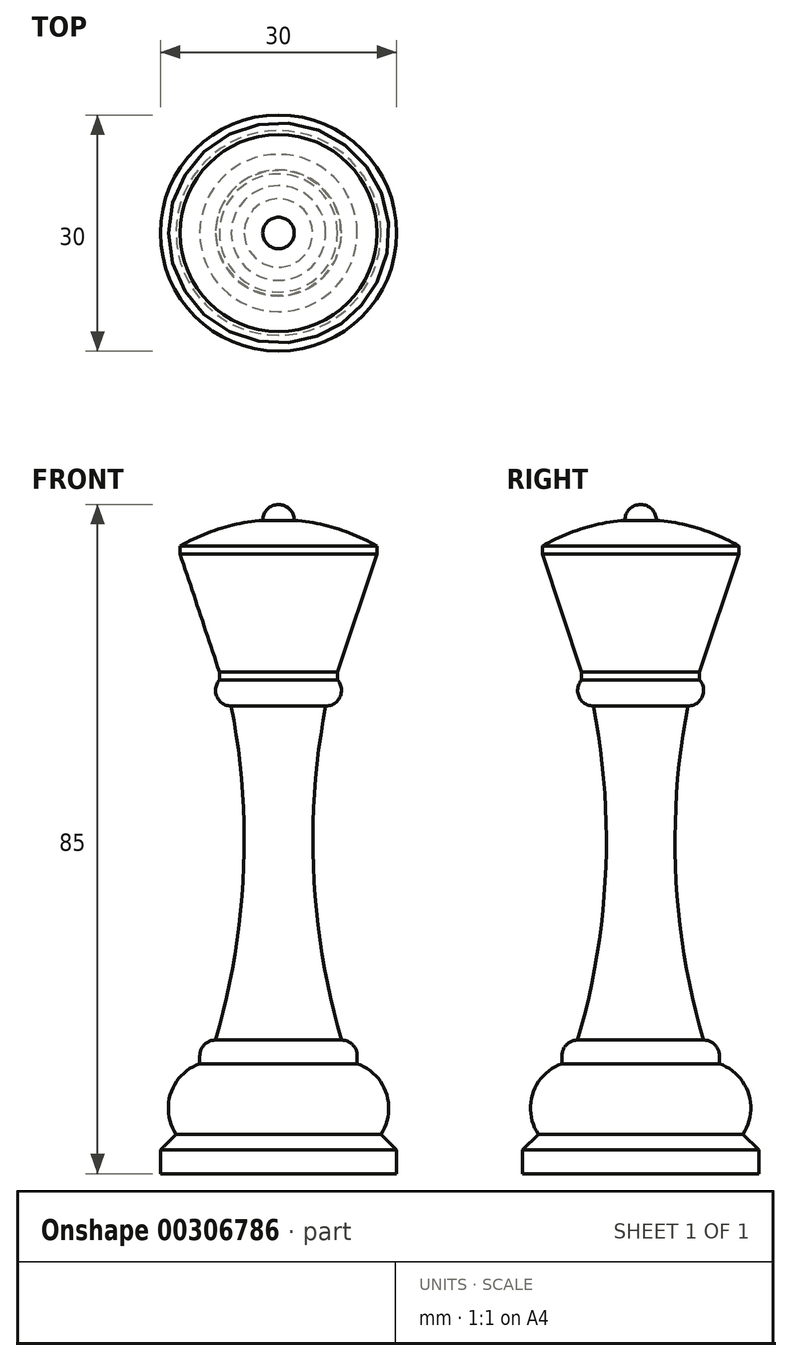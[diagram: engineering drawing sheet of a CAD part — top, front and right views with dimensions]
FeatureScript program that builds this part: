
annotation { "Feature Type Name" : "Feature", "Feature Type Description" : "" }
export const myFeature = defineFeature(function(context is Context, id is Id, definition is map)
    precondition{}
    {
        {
            var Q0;
            Q0=qCreatedBy(makeId("Front.planeOp"),FACE);
            var sketch = newSketch(context, id + "F0", { "sketchPlane" : qUnion([Q0])});
            skArc(sketch, "E0", {"start": v(2, -2) * mm, "mid": v(1.41, -0.59) * mm, "end": v(0, 0) * mm});
            skArc(sketch, "E1", {"start": v(12.5, -5.28) * mm, "mid": v(7.43, -3.05) * mm, "end": v(2, -2) * mm});
            skLineSegment(sketch, "E2", {"start": v(12.5, -5.28) * mm, "end": v(12.5, -6.28) * mm});
            skLineSegment(sketch, "E3", {"start": v(12.5, -6.28) * mm, "end": v(7.5, -21.28) * mm});
            skLineSegment(sketch, "E4", {"start": v(7.5, -21.28) * mm, "end": v(7.5, -22.28) * mm});
            skArc(sketch, "E5", {"start": v(6, -25.6) * mm, "mid": v(7.82, -24.42) * mm, "end": v(7.5, -22.28) * mm});
            skArc(sketch, "E6", {"start": v(6, -25.6) * mm, "mid": v(4.46, -46.93) * mm, "end": v(8, -68.03) * mm});
            skArc(sketch, "E7", {"start": v(10, -70.03) * mm, "mid": v(9.41, -68.61) * mm, "end": v(8, -68.03) * mm});
            skLineSegment(sketch, "E8", {"start": v(10, -70.03) * mm, "end": v(10, -71.03) * mm});
            skArc(sketch, "E9", {"start": v(13, -80) * mm, "mid": v(13.7, -74.78) * mm, "end": v(10, -71.03) * mm});
            skLineSegment(sketch, "E10", {"start": v(13, -80) * mm, "end": v(15, -82) * mm});
            skLineSegment(sketch, "E11", {"start": v(15, -82) * mm, "end": v(15, -85) * mm});
            skLineSegment(sketch, "E12", {"start": v(15, -85) * mm, "end": v(0, -85) * mm});
            skLineSegment(sketch, "E13", {"start": v(0, -85) * mm, "end": v(0, 0) * mm});
            skLineSegment(sketch, "E14", {"start": v(12.5, -5.28) * mm, "end": v(0, -5.28) * mm});
            skLineSegment(sketch, "E15", {"start": v(12.5, -6.28) * mm, "end": v(0, -6.28) * mm});
            skLineSegment(sketch, "E16", {"start": v(7.5, -22.28) * mm, "end": v(0, -22.28) * mm});
            skLineSegment(sketch, "E17", {"start": v(7.5, -21.28) * mm, "end": v(0, -21.28) * mm});
            skLineSegment(sketch, "E18", {"start": v(10, -71.03) * mm, "end": v(0, -71.03) * mm});
            skLineSegment(sketch, "E19", {"start": v(10, -70.03) * mm, "end": v(0, -70.03) * mm});
            skLineSegment(sketch, "E20", {"start": v(15, -82) * mm, "end": v(0, -82) * mm});
            skLineSegment(sketch, "E21", {"start": v(13, -80) * mm, "end": v(0, -80) * mm});
            skLineSegment(sketch, "E22", {"start": v(6, -25.6) * mm, "end": v(0, -25.6) * mm});
            skLineSegment(sketch, "E23", {"start": v(2, -2) * mm, "end": v(0, -2) * mm});
            skLineSegment(sketch, "E24", {"start": v(8, -68.03) * mm, "end": v(0, -68.03) * mm});
            skSolve(sketch);
        }
        {
            var Q0;
            Q0 = qSketchRegion(id + "F0", true);
            var Q1;
            Q1=sQuery(id+"F0.wireOp",EDGE,"E13");
            revolve(context, id + "F1", {"entities" : qUnion([Q0]), "axis" : qUnion([Q1]), "revolveType" : RevolveType.FULL});
        }
    });
